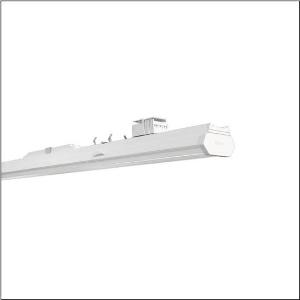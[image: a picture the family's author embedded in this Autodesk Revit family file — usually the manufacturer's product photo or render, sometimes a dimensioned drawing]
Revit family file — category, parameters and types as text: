
# Revit family: licross_11_protected_mo_51td12cn49xg
name_source: partatom
category: Lighting Fixtures
units: mm (PartAtom-declared; Revit-internal decimal feet)

## family parameters
Cut with Voids When Loaded = No
Host = Face
Light Source = No
Part Type = Normal
Room Calculation Point = No
Round Connector Dimension = Use Diameter
Shared = No

## types (1)
- --- (1 x LED, 9070 lm, 49.4 W, 4000K)
    Apparent Load = 49 VA
    CIE Flux Codes = 73 92 98 99 100
    Color Rendering = 80
    Color Temperature = 4000K
    Default Elevation = 1800 mm
    Description = Licross 11 Protected MO, luminaire insert, of sheet steel, galvanised, coil coated, white, length: 1.500mm, width: 90mm, height: 101mm, LED rated luminous flux: 9.070lm, light colour: 840, SDCM (Standard Deviation of Colour Matching)MacAdam ≤ 2 SDCM (initial), control gear: ON/OFF Multilumen, CLOi, with plug, 3-pole, with phase selection, mains connection: 220..240V, AC, 50/60Hz, start of lifetime: 49W, end of service life: 55W, internal wiring halogen-free, primary light control with lens, of plastic, primary optical cover: cover, of PMMA, light emission: direct distribution, primary light characteristic: symmetric, protection rating (complete): IP54, insulation class (complete): insulation class I (protective earthing), certification: CE, ENEC, VDE, UKCA, protection symbol: D if used in an environment with non-conductive dust loads with corresponding accessories, impact resistance: IK06, permissible ambient temperature for indoor applications: -35..+40°C, corresponds to IFS (International Featured Standards) requirements for safety and quality in the food industry, reducing of maximum allowable ambient temperature of 5°C with ceiling mounting, LABS conformity tested according to VDMA 24364:2018-05, The light source and the operating device comply with the requirements of the Ecodesign Regulation (EU) 2019/2020 and are replaceable in accordance with this regulation, packaging unit: 1 piece
    Height = 92 mm
    Lamp = 1 x LED
    Lamp Light Flux = 9070 lm
    Lamp Power = 49.4 W
    Lamp count = 1
    Length = 1500 mm
    Luminous efficacy = 184 lm/W
    Manufacturer = Siteco
    ModVariant = No
    Model = 51TD12CN49XG
    Mounting Place = Ceiling
    Mounting Type = Pendant
    Number of Poles = 1
    OnlyDefault = Yes
    Power Factor = 1
    Product Name = Licross 11 Protected MO
    Product group = luminaire insert | ceiling pendant
    ProductGroupID = 901
    Protection Class = Protection class I
    Protection Degree = IP 54
    RLX_Detail_Level = 1
    RLX_Emergency_Light_Flux = 0 lm
    RLX_Emergency_Type = 0
    RLX_Emergency_Type_DB = No
    RlxData = <blob elided: 22349 chars, md5=a44378ec>
    Socket = socket
    Standby Power = 0 W
    System Light Flux = 9070 lm
    System Power = 49 W
    Type Comments = factory setting: luminous flux: 100 % | (A | C | E) | 113 mA
    Type Image = l_1256145.jpg
    URL = http://relux.com
    VarID = @adj_000847
    Voltage = 0 V
    Weight = 0.00 kg
    Width = 88 mm

## geometry (parser evidence)
native form markers: Blend x4, Sweep x11
no freeform markers — native parametric forms only
